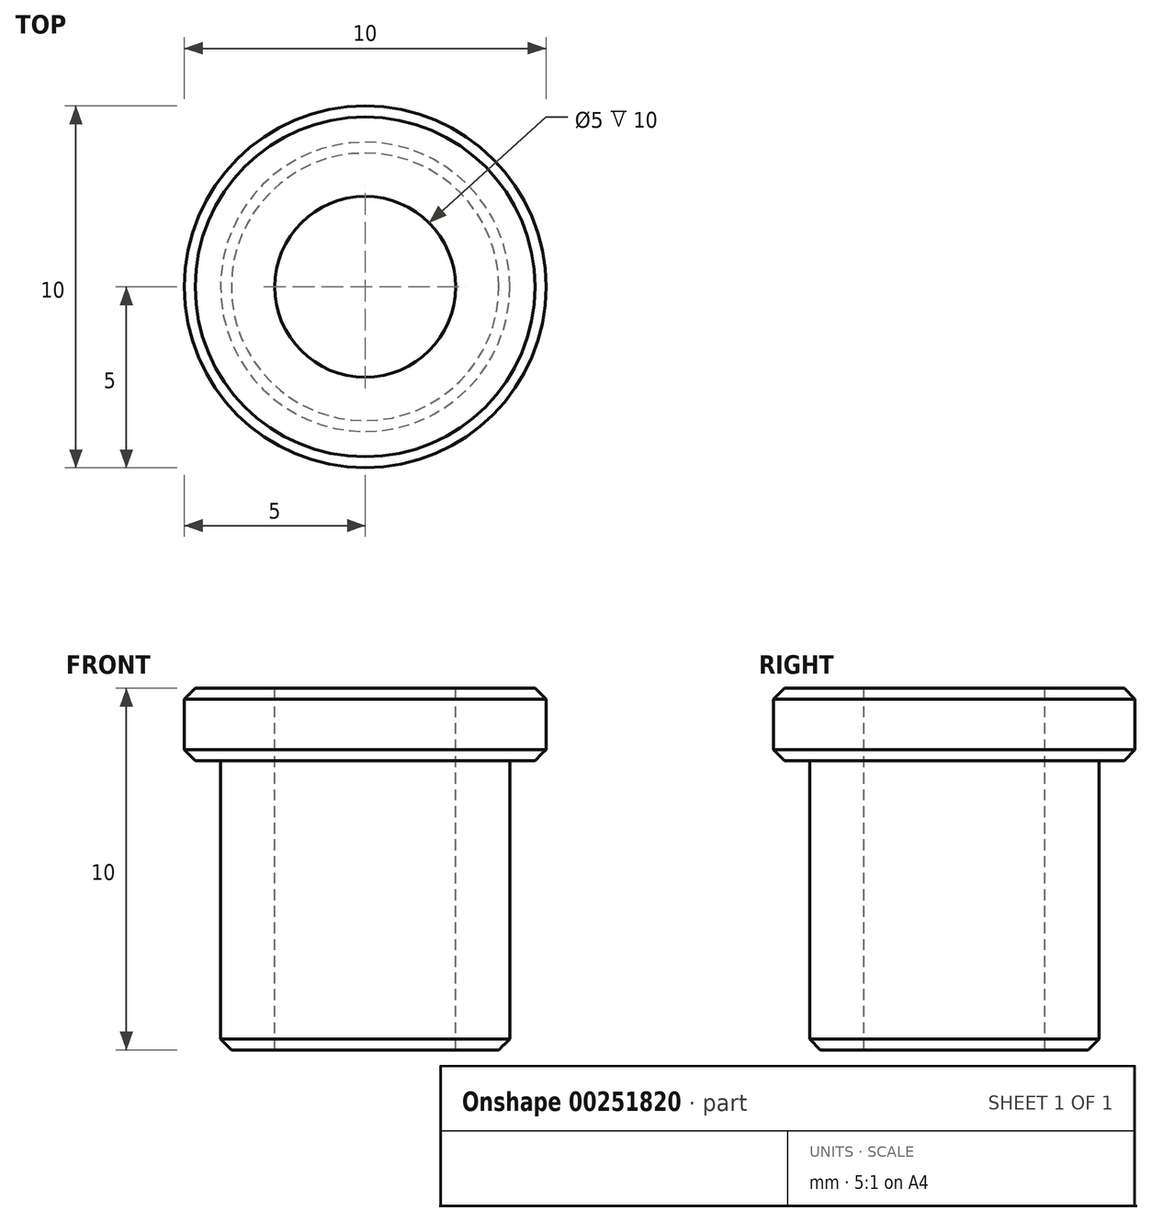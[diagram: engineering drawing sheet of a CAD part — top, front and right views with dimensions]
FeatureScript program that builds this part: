
annotation { "Feature Type Name" : "Feature", "Feature Type Description" : "" }
export const myFeature = defineFeature(function(context is Context, id is Id, definition is map)
    precondition{}
    {
        {
            var Q0;
            Q0=qCreatedBy(makeId("Front.planeOp"),FACE);
            var sketch = newSketch(context, id + "F0", { "sketchPlane" : qUnion([Q0])});
            skLineSegment(sketch, "E0", {"start": v(0, 9.27) * mm, "end": v(0, -8) * mm});
            skLineSegment(sketch, "E1", {"start": v(0, -8) * mm, "end": v(-4, -8) * mm});
            skLineSegment(sketch, "E2", {"start": v(-4, -8) * mm, "end": v(-4, 0) * mm});
            skLineSegment(sketch, "E3", {"start": v(-4, 0) * mm, "end": v(-5, 0) * mm});
            skLineSegment(sketch, "E4", {"start": v(-5, 0) * mm, "end": v(-5, 2) * mm});
            skLineSegment(sketch, "E5", {"start": v(-5, 2) * mm, "end": v(0, 2) * mm});
            skLineSegment(sketch, "E6", {"start": v(0, 2) * mm, "end": v(0, 0) * mm});
            skSolve(sketch);
        }
        {
            var Q0;
            {var subQ0=sQuery(id+"F0.wireOp",EDGE,"E1");Q0=makeQuery(id+"F0.imprint","IMPRINT",FACE,{"disambiguationData":[TD([[makeQuery(id+"F0.imprint","IMPRINT",EDGE,{"derivedFrom":subQ0}),-1.0]])]});}
            var Q1;
            Q1=sQuery(id+"F0.wireOp",EDGE,"E0");
            revolve(context, id + "F1", {"entities" : qUnion([Q0]), "axis" : qUnion([Q1]), "revolveType" : RevolveType.FULL});
        }
        {
            var Q0;
            Q0=makeQuery(id+"F1.opRevolve","SWEPT_FACE",FACE,{"disambiguationData":[OSD([sQuery(id+"F0.wireOp",EDGE,"E5")])]});
            var sketch = newSketch(context, id + "F2", { "sketchPlane" : qUnion([Q0])});
            skCircle(sketch, "E7", {"center": v(0, 0) * mm, "radius": 2.5 * mm});
            skSolve(sketch);
        }
        {
            var Q0;
            Q0 = qSketchRegion(id + "F2", true);
            extrude(context, id + "F3", {"entities" : qUnion([Q0]), "operationType" : NewBodyOperationType.REMOVE, "endBound" : BoundingType.THROUGH_ALL, "oppositeDirection" : true, "depth" : 25 * mm});
        }
        {
            var Q0;
            Q0=makeQuery(id+"F1.opRevolve","SWEPT_EDGE",EDGE,{"disambiguationData":[OSD([sQuery(id+"F0.wireOp",EDGE,"E4"),sQuery(id+"F0.wireOp",EDGE,"E5")])]});
            var Q1;
            Q1=makeQuery(id+"F1.opRevolve","SWEPT_EDGE",EDGE,{"disambiguationData":[OSD([sQuery(id+"F0.wireOp",EDGE,"E3"),sQuery(id+"F0.wireOp",EDGE,"E4")])]});
            var Q2;
            Q2=makeQuery(id+"F1.opRevolve","SWEPT_EDGE",EDGE,{"disambiguationData":[OSD([sQuery(id+"F0.wireOp",EDGE,"E1"),sQuery(id+"F0.wireOp",EDGE,"E2")])]});
            chamfer(context, id + "F4", {"entities" : qUnion([Q0, Q1, Q2]), "width" : .3 * mm, "tangentPropagation" : true});
        }
    });
